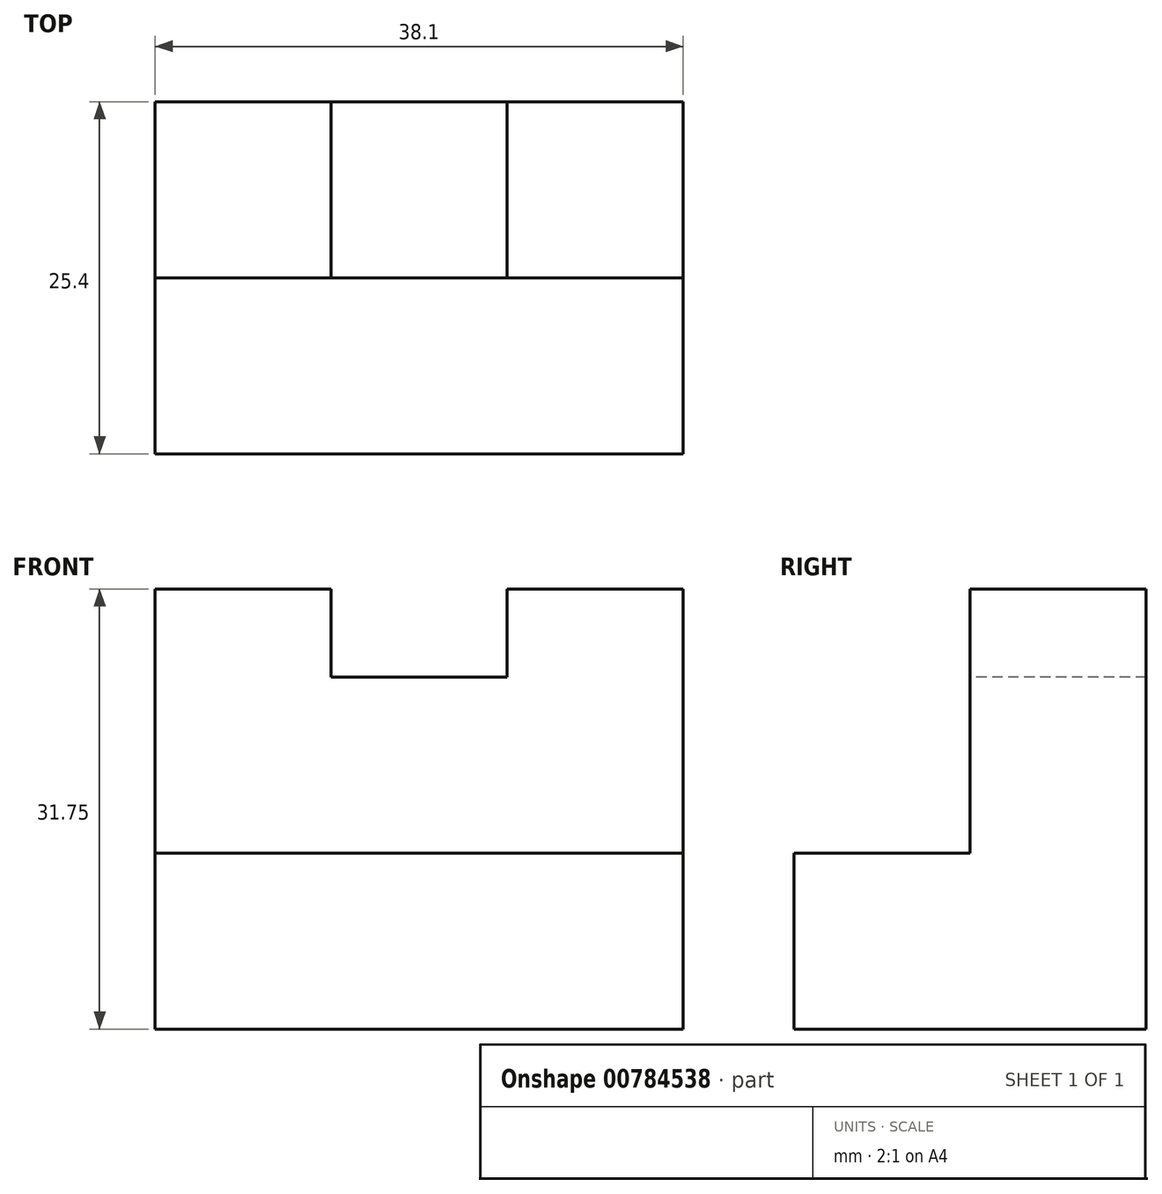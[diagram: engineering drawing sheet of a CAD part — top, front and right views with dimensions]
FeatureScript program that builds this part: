
annotation { "Feature Type Name" : "Feature", "Feature Type Description" : "" }
export const myFeature = defineFeature(function(context is Context, id is Id, definition is map)
    precondition{}
    {
        {
            var Q0;
            Q0=qCreatedBy(makeId("Front.planeOp"),FACE);
            var sketch = newSketch(context, id + "F0", { "sketchPlane" : qUnion([Q0])});
            skLineSegment(sketch, "E0", {"start": v(0, 0) * mm, "end": v(38.1, 0) * mm});
            skLineSegment(sketch, "E1", {"start": v(38.1, 0) * mm, "end": v(38.1, 31.75) * mm});
            skLineSegment(sketch, "E2", {"start": v(38.1, 31.75) * mm, "end": v(0, 31.75) * mm});
            skLineSegment(sketch, "E3", {"start": v(0, 31.75) * mm, "end": v(0, 0) * mm});
            skSolve(sketch);
        }
        {
            var Q0;
            Q0=makeQuery(id+"F0.imprint","IMPRINT",FACE,{"disambiguationData":[TD([[makeQuery(id+"F0.imprint","IMPRINT",EDGE,{"derivedFrom":sQuery(id+"F0.wireOp",EDGE,"E0")}),1.0]])]});
            extrude(context, id + "F1", {"entities" : qUnion([Q0]), "depth" : 25.4 * mm, "offsetDistance" : 25.4 * mm});
        }
        {
            var Q0;
            Q0=makeQuery(id+"F1.opExtrude","SWEPT_FACE",FACE,{"disambiguationData":[OSD([sQuery(id+"F0.wireOp",EDGE,"E1")])]});
            var sketch = newSketch(context, id + "F2", { "sketchPlane" : qUnion([Q0])});
            skLineSegment(sketch, "E4", {"start": v(-25.4, 0) * mm, "end": v(-25.4, 12.7) * mm});
            skLineSegment(sketch, "E5", {"start": v(-25.4, 12.7) * mm, "end": v(-12.7, 12.7) * mm});
            skLineSegment(sketch, "E6", {"start": v(-12.7, 12.7) * mm, "end": v(-12.7, 31.75) * mm});
            skLineSegment(sketch, "E7", {"start": v(-12.7, 31.75) * mm, "end": v(0, 31.75) * mm});
            skLineSegment(sketch, "E8", {"start": v(0, 31.75) * mm, "end": v(0, 0) * mm});
            skLineSegment(sketch, "E9", {"start": v(0, 0) * mm, "end": v(-25.4, 0) * mm});
            skSolve(sketch);
        }
        {
            var Q0;
            {var subQ0=sQuery(id+"F2.wireOp",EDGE,"E5");Q0=makeQuery(id+"F2.imprint","IMPRINT",FACE,{"disambiguationData":[TD([[makeQuery(id+"F2.imprint","IMPRINT",EDGE,{"derivedFrom":subQ0}),1.0]])]});}
            extrude(context, id + "F3", {"entities" : qUnion([Q0]), "operationType" : NewBodyOperationType.REMOVE, "oppositeDirection" : true, "depth" : 38.1 * mm, "offsetDistance" : 25.4 * mm});
        }
        {
            var Q0;
            Q0=makeQuery(id+"F1.opExtrude","SWEPT_FACE",FACE,{"disambiguationData":[OSD([sQuery(id+"F0.wireOp",EDGE,"E2")])]});
            var sketch = newSketch(context, id + "F4", { "sketchPlane" : qUnion([Q0])});
            skLineSegment(sketch, "E10", {"start": v(0, 0) * mm, "end": v(12.7, 0) * mm});
            skLineSegment(sketch, "E11", {"start": v(38.1, 0) * mm, "end": v(25.4, 0) * mm});
            skLineSegment(sketch, "E12", {"start": v(12.7, 0) * mm, "end": v(12.7, -12.7) * mm});
            skLineSegment(sketch, "E13", {"start": v(25.4, 0) * mm, "end": v(25.4, -12.7) * mm});
            skLineSegment(sketch, "E14", {"start": v(12.7, -12.7) * mm, "end": v(25.4, -12.7) * mm});
            skLineSegment(sketch, "E15", {"start": v(12.7, 0) * mm, "end": v(25.4, 0) * mm});
            skSolve(sketch);
        }
        {
            var Q0;
            Q0=makeQuery(id+"F4.imprint","IMPRINT",FACE,{"disambiguationData":[TD([[makeQuery(id+"F4.imprint","IMPRINT",EDGE,{"derivedFrom":sQuery(id+"F4.wireOp",EDGE,"E12")}),1.0]])]});
            extrude(context, id + "F5", {"entities" : qUnion([Q0]), "operationType" : NewBodyOperationType.REMOVE, "oppositeDirection" : true, "depth" : 6.35 * mm, "offsetDistance" : 25.4 * mm});
        }
    });
